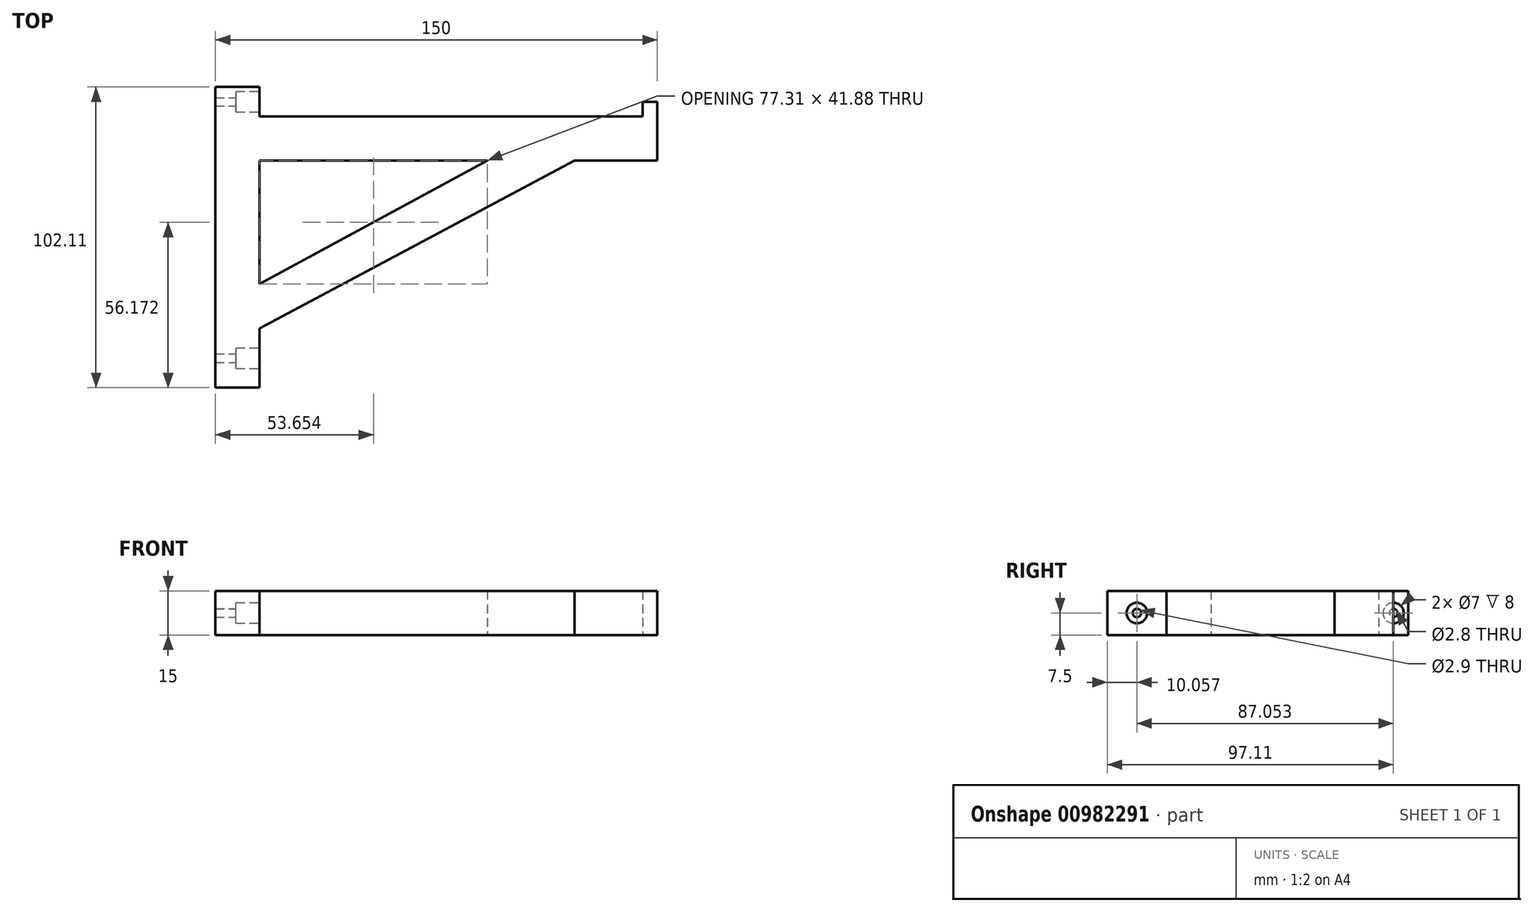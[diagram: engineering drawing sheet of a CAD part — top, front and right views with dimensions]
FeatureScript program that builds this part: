
annotation { "Feature Type Name" : "Feature", "Feature Type Description" : "" }
export const myFeature = defineFeature(function(context is Context, id is Id, definition is map)
    precondition{}
    {
        {
            var Q0;
            Q0=qCreatedBy(makeId("Top.planeOp"),FACE);
            var sketch = newSketch(context, id + "F0", { "sketchPlane" : qUnion([Q0])});
            skLineSegment(sketch, "E0", {"start": v(0, 0) * mm, "end": v(0, 80) * mm});
            skLineSegment(sketch, "E1", {"start": v(0, 80) * mm, "end": v(150, 80) * mm});
            skLineSegment(sketch, "E2", {"start": v(0, 0) * mm, "end": v(0, 15) * mm, "construction": true});
            skLineSegment(sketch, "E3", {"start": v(150, 80) * mm, "end": v(120, 80) * mm, "construction": true});
            skLineSegment(sketch, "E4", {"start": v(120, 80) * mm, "end": v(0, 15) * mm});
            skLineSegment(sketch, "E5", {"start": v(150, 80) * mm, "end": v(0, 0) * mm});
            skLineSegment(sketch, "E6", {"start": v(0, 0) * mm, "end": v(0, -12.1) * mm});
            skLineSegment(sketch, "E7", {"start": v(0, -12.1) * mm, "end": v(15, -12.1) * mm});
            skLineSegment(sketch, "E8", {"start": v(15, -12.1) * mm, "end": v(15, 80) * mm});
            skLineSegment(sketch, "E9", {"start": v(0, 80) * mm, "end": v(0, 65) * mm, "construction": true});
            skLineSegment(sketch, "E10", {"start": v(0, 65) * mm, "end": v(92.3, 65) * mm});
            skLineSegment(sketch, "E11", {"start": v(150, 80) * mm, "end": v(150, 65) * mm});
            skLineSegment(sketch, "E12", {"start": v(150, 65) * mm, "end": v(92.3, 65) * mm});
            skLineSegment(sketch, "E13", {"start": v(0, 80) * mm, "end": v(0, 90) * mm});
            skLineSegment(sketch, "E14", {"start": v(0, 90) * mm, "end": v(15, 90) * mm});
            skLineSegment(sketch, "E15", {"start": v(15, 90) * mm, "end": v(15, 80) * mm});
            skLineSegment(sketch, "E16.bottom", {"start": v(150, 80) * mm, "end": v(145, 80) * mm});
            skLineSegment(sketch, "E16.top", {"start": v(150, 85) * mm, "end": v(145, 85) * mm});
            skLineSegment(sketch, "E16.left", {"start": v(150, 80) * mm, "end": v(150, 85) * mm});
            skLineSegment(sketch, "E16.right", {"start": v(145, 80) * mm, "end": v(145, 85) * mm});
            skSolve(sketch);
        }
        {
            var Q0;
            {var subQ0=sQuery(id+"F0.wireOp",EDGE,"E4");var subQ1=sQuery(id+"F0.wireOp",EDGE,"E0");var subQ2=makeQuery(id+"F0.imprint","INTERSECT",VERTEX,{"derivedFrom":[subQ1,subQ0]});Q0=makeQuery(id+"F0.imprint","IMPRINT",FACE,{"disambiguationData":[TD([[makeQuery(id+"F0.imprint","IMPRINT",EDGE,{"disambiguationData":[TD([[subQ2,1.0]])],"derivedFrom":subQ0}),1.0]])]});}
            var Q1;
            {var subQ0=sQuery(id+"F0.wireOp",EDGE,"E4");var subQ1=sQuery(id+"F0.wireOp",EDGE,"E0");var subQ2=makeQuery(id+"F0.imprint","INTERSECT",VERTEX,{"derivedFrom":[subQ1,subQ0]});Q1=makeQuery(id+"F0.imprint","IMPRINT",FACE,{"disambiguationData":[TD([[makeQuery(id+"F0.imprint","IMPRINT",EDGE,{"disambiguationData":[TD([[subQ2,-1.0]])],"derivedFrom":subQ1}),-1.0]])]});}
            var Q2;
            {var subQ0=sQuery(id+"F0.wireOp",EDGE,"E12");var subQ5=sQuery(id+"F0.wireOp",EDGE,"E5");var subQ7=makeQuery(id+"F0.imprint","INTERSECT",VERTEX,{"derivedFrom":[subQ5,subQ0]});Q2=makeQuery(id+"F0.imprint","IMPRINT",FACE,{"disambiguationData":[TD([[makeQuery(id+"F0.imprint","IMPRINT",EDGE,{"disambiguationData":[TD([[subQ7,-1.0]])],"derivedFrom":subQ5}),-1.0]])]});}
            var Q3;
            {var subQ0=sQuery(id+"F0.wireOp",EDGE,"E6");Q3=makeQuery(id+"F0.imprint","IMPRINT",FACE,{"disambiguationData":[TD([[makeQuery(id+"F0.imprint","IMPRINT",EDGE,{"derivedFrom":subQ0}),1.0]])]});}
            var Q4;
            {var subQ1=sQuery(id+"F0.wireOp",EDGE,"E1");var subQ3=sQuery(id+"F0.wireOp",EDGE,"E4");var subQ4=makeQuery(id+"F0.imprint","INTERSECT",VERTEX,{"derivedFrom":[subQ1,subQ3]});Q4=makeQuery(id+"F0.imprint","IMPRINT",FACE,{"disambiguationData":[TD([[makeQuery(id+"F0.imprint","IMPRINT",EDGE,{"disambiguationData":[TD([[subQ4,1.0]])],"derivedFrom":subQ1}),-1.0]])]});}
            var Q5;
            {var subQ3=sQuery(id+"F0.wireOp",EDGE,"E10");var subQ5=sQuery(id+"F0.wireOp",EDGE,"E8");var subQ7=makeQuery(id+"F0.imprint","INTERSECT",VERTEX,{"derivedFrom":[subQ5,subQ3]});Q5=makeQuery(id+"F0.imprint","IMPRINT",FACE,{"disambiguationData":[TD([[makeQuery(id+"F0.imprint","IMPRINT",EDGE,{"disambiguationData":[TD([[subQ7,1.0]])],"derivedFrom":subQ3}),1.0]])]});}
            var Q6;
            {var subQ0=sQuery(id+"F0.wireOp",EDGE,"E13");Q6=makeQuery(id+"F0.imprint","IMPRINT",FACE,{"disambiguationData":[TD([[makeQuery(id+"F0.imprint","IMPRINT",EDGE,{"derivedFrom":subQ0}),-1.0]])]});}
            var Q7;
            {var subQ3=sQuery(id+"F0.wireOp",EDGE,"E1");var subQ8=makeQuery(id+"F0.imprint","INTERSECT",VERTEX,{"derivedFrom":[subQ3,sQuery(id+"F0.wireOp",EDGE,"E16.right")]});Q7=makeQuery(id+"F0.imprint","IMPRINT",FACE,{"disambiguationData":[TD([[makeQuery(id+"F0.imprint","IMPRINT",EDGE,{"disambiguationData":[TD([[subQ8,1.0]])],"derivedFrom":subQ3}),-1.0]])]});}
            var Q8;
            {var subQ0=sQuery(id+"F0.wireOp",EDGE,"E11");Q8=makeQuery(id+"F0.imprint","IMPRINT",FACE,{"disambiguationData":[TD([[makeQuery(id+"F0.imprint","IMPRINT",EDGE,{"derivedFrom":subQ0}),-1.0]])]});}
            var Q9;
            Q9=makeQuery(id+"F0.imprint","IMPRINT",FACE,{"disambiguationData":[TD([[makeQuery(id+"F0.imprint","IMPRINT",EDGE,{"derivedFrom":sQuery(id+"F0.wireOp",EDGE,"E16.top")}),1.0]])]});
            extrude(context, id + "F1", {"entities" : qUnion([Q0, Q1, Q2, Q3, Q4, Q5, Q6, Q7, Q8, Q9]), "depth" : 15 * mm, "offsetDistance" : 25 * mm});
        }
        {
            var Q0;
            Q0=makeQuery(id+"F1.opExtrude","SWEPT_FACE",FACE,{"disambiguationData":[OSD([sQuery(id+"F0.wireOp",EDGE,"E15")])]});
            var sketch = newSketch(context, id + "F2", { "sketchPlane" : qUnion([Q0])});
            skCircle(sketch, "E17", {"center": v(85, 7.5) * mm, "radius": 3.5 * mm});
            skPoint(sketch, "E17.centerSnap0", {"position": v(85, 15) * mm});
            skPoint(sketch, "E17.centerSnap1", {"position": v(90, 7.5) * mm});
            skCircle(sketch, "E18", {"center": v(85, 7.5) * mm, "radius": 1.4 * mm});
            skSolve(sketch);
        }
        {
            var Q0;
            Q0=makeQuery(id+"F2.imprint","IMPRINT",FACE,{"disambiguationData":[TD([[makeQuery(id+"F2.imprint","IMPRINT",EDGE,{"derivedFrom":sQuery(id+"F2.wireOp",EDGE,"E18")}),1.0]])]});
            extrude(context, id + "F3", {"entities" : qUnion([Q0]), "operationType" : NewBodyOperationType.REMOVE, "oppositeDirection" : true, "depth" : 25 * mm, "offsetDistance" : 25 * mm});
        }
        {
            var Q0;
            Q0=makeQuery(id+"F2.imprint","IMPRINT",FACE,{"disambiguationData":[TD([[makeQuery(id+"F2.imprint","IMPRINT",EDGE,{"derivedFrom":sQuery(id+"F2.wireOp",EDGE,"E17")}),1.0]])]});
            extrude(context, id + "F4", {"entities" : qUnion([Q0]), "operationType" : NewBodyOperationType.REMOVE, "oppositeDirection" : true, "depth" : 8 * mm, "offsetDistance" : 25 * mm});
        }
        {
            var Q0;
            {var subQ0=sQuery(id+"F0.wireOp",EDGE,"E8");Q0=makeQuery(id+"F1.opExtrude","SWEPT_FACE",FACE,{"disambiguationData":[OSD([subQ0]),TDD([makeQuery(id+"F0.imprint","IMPRINT",EDGE,{"disambiguationData":[TD([[makeQuery(id+"F0.imprint","INTERSECT",VERTEX,{"derivedFrom":[sQuery(id+"F0.wireOp",EDGE,"E7"),subQ0]}),-1.0]])],"derivedFrom":subQ0})])]});}
            var sketch = newSketch(context, id + "F5", { "sketchPlane" : qUnion([Q0])});
            skCircle(sketch, "E19", {"center": v(-2.05, 7.5) * mm, "radius": 3.5 * mm});
            skPoint(sketch, "E19.centerSnap0", {"position": v(-2.05, 15) * mm});
            skPoint(sketch, "E19.centerSnap1", {"position": v(-12.1, 7.5) * mm});
            skCircle(sketch, "E20", {"center": v(-2.05, 7.5) * mm, "radius": 1.45 * mm});
            skSolve(sketch);
        }
        {
            var Q0;
            Q0=makeQuery(id+"F5.imprint","IMPRINT",FACE,{"disambiguationData":[TD([[makeQuery(id+"F5.imprint","IMPRINT",EDGE,{"derivedFrom":sQuery(id+"F5.wireOp",EDGE,"E19")}),1.0]])]});
            extrude(context, id + "F6", {"entities" : qUnion([Q0]), "operationType" : NewBodyOperationType.REMOVE, "oppositeDirection" : true, "depth" : 8 * mm, "offsetDistance" : 25 * mm});
        }
        {
            var Q0;
            {var subQ0=sQuery(id+"F0.wireOp",EDGE,"E8");Q0=makeQuery(id+"F6.boolean.opBoolean","SPLIT",FACE,{"disambiguationData":[TD([makeQuery(id+"F6.opExtrude","SWEPT_FACE",FACE,{"disambiguationData":[OSD([sQuery(id+"F5.wireOp",EDGE,"E20")])]})])],"derivedFrom":makeQuery(id+"F1.opExtrude","SWEPT_FACE",FACE,{"disambiguationData":[OSD([subQ0]),TDD([makeQuery(id+"F0.imprint","IMPRINT",EDGE,{"disambiguationData":[TD([[makeQuery(id+"F0.imprint","INTERSECT",VERTEX,{"derivedFrom":[sQuery(id+"F0.wireOp",EDGE,"E7"),subQ0]}),-1.0]])],"derivedFrom":subQ0})])]})});}
            extrude(context, id + "F7", {"entities" : qUnion([Q0]), "operationType" : NewBodyOperationType.REMOVE, "oppositeDirection" : true, "depth" : 25 * mm, "offsetDistance" : 25 * mm});
        }
    });
